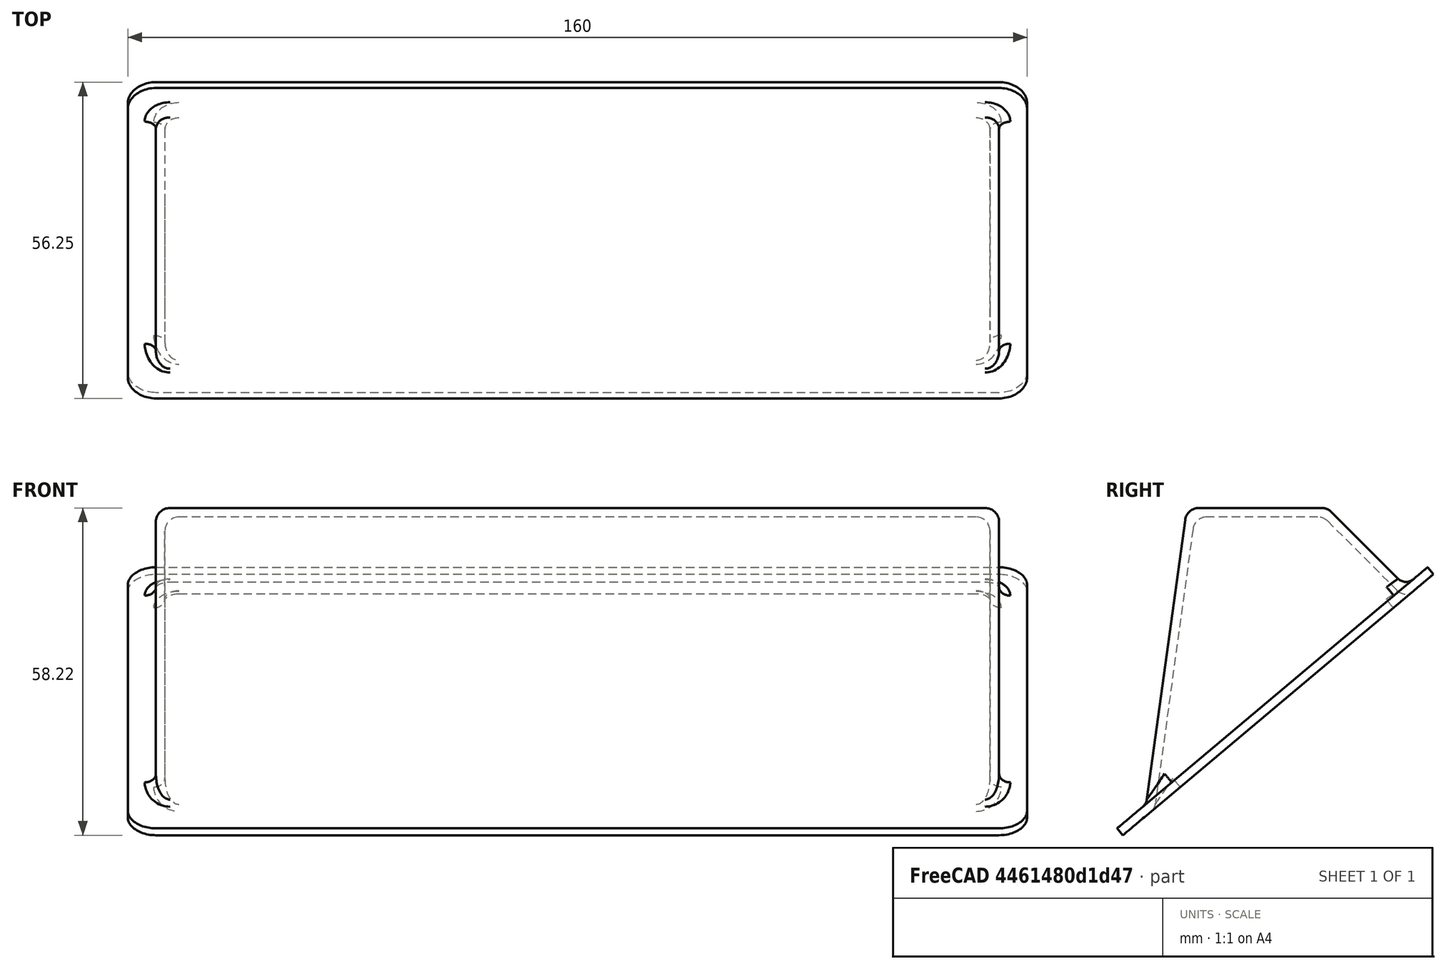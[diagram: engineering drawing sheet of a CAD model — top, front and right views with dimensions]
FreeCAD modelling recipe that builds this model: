
FCSTD DOCUMENT  (FreeCAD 0.22R36807 (Git))
Label: pottle2
License: All rights reserved
LicenseURL: http://en.wikipedia.org/wiki/All_rights_reserved
objects: TechDraw::DrawViewDimension×9, TechDraw::DrawViewBalloon×4, Sketcher::SketchObject×3, PartDesign::FeatureSubtractivePython×3, PartDesign::Pad×2, PartDesign::Fillet×2, Part::FeaturePython×2, App::LinkElement×2, Part::Part2DObjectPython×1, PartDesign::SubShapeBinder×1, PartDesign::Thickness×1, PartDesign::FeaturePython×1, PartDesign::Body×1, TechDraw::DrawSVGTemplate×1, App::DocumentObjectGroup×1, TechDraw::DrawViewPart×1, TechDraw::DrawViewSection×1, TechDraw::DrawPage×1
note: 42 computed .brp shape members not serialized (recipe doc carries the construction recipe); baked Part::Feature solids carry a one-line shape summary decoded from their .brp

FEATURE [Sketcher::SketchObject] Sketch
  FullyConstrained = true
  Placement = pos=(0,0,0) rot=(0.57735,0.57735,0.57735;2.0944rad)
  sketch-geometry (9):
    g0: LineSegment StartX=-31.3593 StartY=11.7819 StartZ=0 EndX=-27.5326 EndY=15 EndZ=0
    g1: LineSegment StartX=-27.5326 StartY=15 StartZ=0 EndX=-12.5 EndY=0 EndZ=0
    g2: LineSegment StartX=-12.5 StartY=0 StartZ=0 EndX=12.5 EndY=0 EndZ=0
    g3: LineSegment StartX=12.5 StartY=0 StartZ=0 EndX=20.0326 EndY=55 EndZ=0
    g4: LineSegment StartX=20.0326 StartY=55 StartZ=0 EndX=23.8593 EndY=58.2181 EndZ=0
    g5: LineSegment StartX=-27.5326 StartY=15 StartZ=0 EndX=20.0326 EndY=55 EndZ=0
    g6: LineSegment StartX=-27.5326 StartY=15 StartZ=0 EndX=-20 EndY=70 EndZ=0
    g7: LineSegment StartX=-20 StartY=70 StartZ=0 EndX=5 EndY=70 EndZ=0
    g8: LineSegment StartX=5 StartY=70 StartZ=0 EndX=20.0326 EndY=55 EndZ=0
  constraints (28):
    c: Coincident(g0,g1)
    c: PointOnObject(g1,g-1)
    c: Coincident(g1,g2)
    c: Coincident(g2,g3)
    c: Coincident(g3,g4)
    c: Equal(g4,g0)
    c: Angle(g0,g1) = 1.65806
    c: Distance(g0,g0) = 5
    c: DistanceX(g2,g2) = 25
    c: Coincident(g5,g0)
    c: Coincident(g5,g3)
    c: Parallel(g0,g5)
    c: Parallel(g5,g4)
    c: DistanceY(g0) = 15
    c: Angle(g2,g1) = 2.35728
    c: Angle(g3,g2) = 1.70691
    c: Distance(g0,g4) = 72.1486
    c: Symmetric(g1,g2,g-2)
    c: Coincident(g0,g6)
    c: Coincident(g6,g7)
    c: Horizontal(g7)
    c: Coincident(g7,g8)
    c: Coincident(g8,g3)
    c: Equal(g8,g1)
    c: Equal(g7,g2)
    c: Equal(g6,g3)
    c: DistanceY(g6) = 70
    c: DistanceX(g7) = 5
FEATURE [Part::Part2DObjectPython] Clone2D  label="Sketch (2D)"  # Draft 2D object (typed FeaturePython)
  Fuse = false
  Objects = -> [Sketch]
  Placement = pos=(7e-15,70.8395,36.5891) rot=(0.57735,0.57735,0.57735;2.0944rad)
  Scale = (1,1,1)
FEATURE [PartDesign::SubShapeBinder] Binder
  BindCopyOnChange = 0
  BindMode = 0
  ClaimChildren = true
  Context = -> Body [Binder.]
  Fuse = false
  MakeFace = true
  OffsetFill = false
  OffsetIntersection = false
  OffsetJoinType = 0
  OffsetOpenResult = false
  PartialLoad = false
  Relative = true
  Support = -> [Sketch]
  _Version = 2
FEATURE [Sketcher::SketchObject] Sketch001
  AttachmentSupport = -> [YZ_Plane]
  ExternalGeometry = -> [Binder]
  FullyConstrained = true
  MapMode = 5
  Placement = pos=(0,0,0) rot=(0.57735,0.57735,0.57735;2.0944rad)
  sketch-geometry (4):
    g0: LineSegment StartX=-12.5 StartY=-1.8e-15 StartZ=0 EndX=12.5 EndY=0 EndZ=0
    g1: LineSegment StartX=12.5 StartY=0 StartZ=0 EndX=20.0326 EndY=55 EndZ=0
    g2: LineSegment StartX=20.0326 StartY=55 StartZ=0 EndX=-27.5326 EndY=15 EndZ=0
    g3: LineSegment StartX=-27.5326 StartY=15 StartZ=0 EndX=-12.5 EndY=-1.8e-15 EndZ=0
  constraints (8):
    c: Coincident(g-3,g0)
    c: Coincident(g0,g-4)
    c: Coincident(g0,g1)
    c: Coincident(g1,g-4)
    c: Coincident(g1,g2)
    c: Coincident(g2,g-3)
    c: Coincident(g2,g3)
    c: Coincident(g3,g0)
FEATURE [PartDesign::Pad] Pad
  Direction = (1,0,0)
  Length = 150
  Length2 = 10
  Midplane = true
  Placement = pos=(0,0,0) rot=(0.57735,0.57735,0.57735;2.0944rad)
  Profile = -> Sketch001
  ReferenceAxis = -> Sketch001 [N_Axis]
  Suppressed = false
  Type = 0
FEATURE [Sketcher::SketchObject] Sketch002
  AttachmentOffset = pos=(0,0,0) rot=(-1,0,0;1.5708rad)
  AttachmentSupport = -> [Binder]
  ExternalGeometry = -> [Binder]
  FullyConstrained = true
  MapMode = 7
  Placement = pos=(0,-27.5326,15) rot=(1,0,0;0.699217rad)
  sketch-geometry (13):
    g0: LineSegment StartX=-75 StartY=-5 StartZ=0 EndX=75 EndY=-5 EndZ=0
    g1: LineSegment StartX=80 StartY=-4e-16 StartZ=0 EndX=80 EndY=62.1486 EndZ=0
    g2: LineSegment StartX=75 StartY=67.1486 StartZ=0 EndX=-75 EndY=67.1486 EndZ=0
    g3: LineSegment StartX=-80 StartY=62.1486 StartZ=0 EndX=-80 EndY=0 EndZ=0
    g4: ArcOfCircle CenterX=-75 CenterY=-5e-16 CenterZ=0 NormalX=0 NormalY=0 NormalZ=1 AngleXU=0 Radius=5 StartAngle=3.14159 EndAngle=4.71239
    g5: ArcOfCircle CenterX=75 CenterY=-3e-16 CenterZ=0 NormalX=0 NormalY=0 NormalZ=1 AngleXU=0 Radius=5 StartAngle=4.71239 EndAngle=6.28319
    g6: ArcOfCircle CenterX=75 CenterY=62.1486 CenterZ=0 NormalX=0 NormalY=0 NormalZ=1 AngleXU=0 Radius=5 StartAngle=-9e-16 EndAngle=1.5708
    g7: ArcOfCircle CenterX=-75 CenterY=62.1486 CenterZ=0 NormalX=0 NormalY=0 NormalZ=1 AngleXU=0 Radius=5 StartAngle=1.5708 EndAngle=3.14159
    g8: GeomPoint X=-80 Y=-5 Z=0
    g9: GeomPoint X=80 Y=67.1486 Z=0
    g10: LineSegment StartX=0 StartY=62.1486 StartZ=0 EndX=0 EndY=67.1486 EndZ=0
    g11: LineSegment StartX=0 StartY=0 StartZ=0 EndX=0 EndY=-5 EndZ=0
    g12: GeomPoint X=0 Y=31.0743 Z=0
  constraints (31):
    c: Tangent(g0,g4) = -1.5708
    c: Tangent(g0,g5) = -1.5708
    c: Tangent(g1,g5) = -1.5708
    c: Tangent(g1,g6) = -1.5708
    c: Tangent(g2,g6) = -1.5708
    c: Tangent(g2,g7) = -1.5708
    c: Tangent(g3,g7) = -1.5708
    c: Tangent(g3,g4) = -1.5708
    c: Horizontal(g0)
    c: Horizontal(g2)
    c: Vertical(g1)
    c: Vertical(g3)
    c: Equal(g4,g5)
    c: Equal(g5,g6)
    c: Equal(g6,g7)
    c: PointOnObject(g8,g0)
    c: PointOnObject(g8,g3)
    c: PointOnObject(g9,g1)
    c: PointOnObject(g9,g2)
    c: Radius(g5) = 5
    c: Coincident(g10,g-3)
    c: PointOnObject(g10,g2)
    c: Coincident(g11,g-1)
    c: PointOnObject(g11,g0)
    c: Vertical(g11)
    c: Equal(g11,g10)
    c: PointOnObject(g12,g-2)
    c: Symmetric(g8,g9,g12)
    c: DistanceX(g8,g9) = 160
    c: DistanceY(g11,g11) = 5
    c: Vertical(g10)
FEATURE [PartDesign::Thickness] Thickness
  Base = -> Pad [Face3]
  BaseFeature = -> Pad
  Intersection = false
  Join = 0
  Mode = 0
  Reversed = true
  SupportTransform = false
  Suppressed = false
  Value = 1.6
FEATURE [PartDesign::FeatureSubtractivePython] PDW_Sub  # link proxy (typed FeaturePython)
  BaseFeature = -> Thickness
  Body = Body
  ClaimChildren = false
  EditPlacementAdjustments = false
  Enabled = 1
  LinkedObject = -> Thickness
  MeshTolerance = 0.1
  PatternBase = -> Pad
  PatternBaseOffset = 0
  PatternBaseScale = 1
  PatternBaseScaleXYZ = (1,1,1)
  PatternOffsetCut = false
  PatternOffsetIntersection = false
  PatternOffsetJoin = 0
  PatternOffsetMode = 0
  PatternOffsetSelfIntersection = false
  PatternOperation = 0
  PatternOperationDefault = None
  PatternScaleCut = false
  PatternShapeOffset = 0
  PatternShapeScale = 1
  PatternShapeScaleXYZ = (1,1,1)
  PatternTool = -> Thickness
  PatternToolOffset = 0
  PatternToolScale = 1
  PatternToolScaleXYZ = (1,1,1)
  RefineMesh = true
  ShapeManagement = 1
  ShowMeshProps = false
  ShowOffsetProps = false
  ShowScaleProps = false
  ShowWarnings = true
  Suppressed = false
  TipBase = -> Pad
  TipBaseOffset = 0
  TipBaseScale = 1
  TipBaseScaleXYZ = (1,1,1)
  TipOffsetCut = false
  TipOffsetIntersection = false
  TipOffsetJoin = 0
  TipOffsetMode = 0
  TipOffsetSelfIntersection = false
  TipOperation = 1
  TipOperationDefault = Cut
  TipScaleCut = false
  TipShapeOffset = 0
  TipShapeScale = 1
  TipShapeScaleXYZ = (1,1,1)
  TipTool = -> Thickness
  TipToolOffset = 0
  TipToolScale = 1
  TipToolScaleXYZ = (1,1,1)
  Type = Subtractive
  UsePatternBaseAddSubShape = false
  UsePatternToolAddSubShape = true
  UseTipBaseAddSubShape = false
  UseTipToolAddSubShape = false
  Version = 0.2023.08.13
FEATURE [PartDesign::FeatureSubtractivePython] PDW_Sub001  # link proxy (typed FeaturePython)
  BaseFeature = -> PDW_Sub
  Body = Body
  ClaimChildren = false
  EditPlacementAdjustments = false
  Enabled = 1
  LinkedObject = -> PDW_Sub
  MeshTolerance = 0.1
  PatternBase = -> Thickness
  PatternBaseOffset = 0
  PatternBaseScale = 1
  PatternBaseScaleXYZ = (1,1,1)
  PatternOffsetCut = false
  PatternOffsetIntersection = false
  PatternOffsetJoin = 0
  PatternOffsetMode = 0
  PatternOffsetSelfIntersection = false
  PatternOperation = 0
  PatternOperationDefault = None
  PatternScaleCut = false
  PatternShapeOffset = 0
  PatternShapeScale = 1
  PatternShapeScaleXYZ = (1,1,1)
  PatternTool = -> PDW_Sub
  PatternToolOffset = 0
  PatternToolScale = 1
  PatternToolScaleXYZ = (1,1,1)
  RefineMesh = true
  ShapeManagement = 0
  ShowMeshProps = false
  ShowOffsetProps = false
  ShowScaleProps = false
  ShowWarnings = true
  Suppressed = false
  TipBase = -> Thickness
  TipBaseOffset = 0
  TipBaseScale = 1
  TipBaseScaleXYZ = (1,1,1)
  TipOffsetCut = false
  TipOffsetIntersection = false
  TipOffsetJoin = 0
  TipOffsetMode = 0
  TipOffsetSelfIntersection = false
  TipOperation = 1
  TipOperationDefault = Cut
  TipScaleCut = false
  TipShapeOffset = 0
  TipShapeScale = 1
  TipShapeScaleXYZ = (1,1,1)
  TipTool = -> PDW_Sub
  TipToolOffset = 0
  TipToolScale = 1
  TipToolScaleXYZ = (1,1,1)
  Type = Subtractive
  UsePatternBaseAddSubShape = false
  UsePatternToolAddSubShape = true
  UseTipBaseAddSubShape = false
  UseTipToolAddSubShape = true
  Version = 0.2023.08.13
FEATURE [PartDesign::Pad] Pad001
  BaseFeature = -> PDW_Sub001
  Direction = (0,-0.643619,0.765346)
  Length = 1.6
  Length2 = 10
  Profile = -> Sketch002
  ReferenceAxis = -> Sketch002 [N_Axis]
  Refine = true
  Reversed = true
  Suppressed = false
  Type = 0
  expr: Length = <<Thickness>>.Value
FEATURE [PartDesign::FeatureSubtractivePython] PDW_Sub002  # link proxy (typed FeaturePython)
  BaseFeature = -> Pad001
  Body = Body
  ClaimChildren = false
  EditPlacementAdjustments = false
  Enabled = 1
  LinkedObject = -> PDW_Sub
  MeshTolerance = 0.1
  PatternBase = -> Pad001
  PatternBaseOffset = 0
  PatternBaseScale = 1
  PatternBaseScaleXYZ = (1,1,1)
  PatternOffsetCut = false
  PatternOffsetIntersection = false
  PatternOffsetJoin = 0
  PatternOffsetMode = 0
  PatternOffsetSelfIntersection = false
  PatternOperation = 0
  PatternOperationDefault = None
  PatternScaleCut = false
  PatternShapeOffset = 0
  PatternShapeScale = 1
  PatternShapeScaleXYZ = (1,1,1)
  PatternTool = -> PDW_Sub
  PatternToolOffset = 0
  PatternToolScale = 1
  PatternToolScaleXYZ = (1,1,1)
  RefineMesh = false
  ShapeManagement = 1
  ShowMeshProps = false
  ShowOffsetProps = false
  ShowScaleProps = false
  ShowWarnings = true
  Suppressed = false
  TipBase = -> Pad001
  TipBaseOffset = 0
  TipBaseScale = 1
  TipBaseScaleXYZ = (1,1,1)
  TipOffsetCut = false
  TipOffsetIntersection = false
  TipOffsetJoin = 0
  TipOffsetMode = 0
  TipOffsetSelfIntersection = false
  TipOperation = 1
  TipOperationDefault = Cut
  TipScaleCut = false
  TipShapeOffset = 0
  TipShapeScale = 1
  TipShapeScaleXYZ = (1,1,1)
  TipTool = -> PDW_Sub
  TipToolOffset = 0
  TipToolScale = 1
  TipToolScaleXYZ = (1,1,1)
  Type = Subtractive
  UsePatternBaseAddSubShape = false
  UsePatternToolAddSubShape = true
  UseTipBaseAddSubShape = false
  UseTipToolAddSubShape = false
  Version = 0.2023.08.13
FEATURE [PartDesign::FeaturePython] Extend  # WARN: FeaturePython — macro-defined, semantics opaque (R4)
  BaseFeature = -> PDW_Sub002
  Offset = 0.02
  Refine = true
  Suppressed = false
  UseSubtraction = false
  baseObject = -> PDW_Sub002 [Face1]
  gap1 = 0
  gap2 = 0
  length = 0
FEATURE [PartDesign::Fillet] Fillet
  Base = -> Extend [Edge46,Edge43,Edge42,Edge45,Edge48,Edge47,Edge44,Edge41,Edge6,Edge4,Edge10,Edge2,Edge8,Edge3,Edge1,Edge5]
  BaseFeature = -> Extend
  Radius = 2.5
  SupportTransform = false
  Suppressed = false
  UseAllEdges = false
FEATURE [PartDesign::Fillet] Fillet001
  Base = -> Fillet [Edge69,Edge26]
  BaseFeature = -> Fillet
  Radius = 2
  SupportTransform = false
  Suppressed = false
  UseAllEdges = false
FEATURE [PartDesign::Body] Body
  Group = -> [Sketch001,Binder,Pad,Sketch002,Thickness,PDW_Sub,PDW_Sub001,Pad001,PDW_Sub002,Extend,Fillet,Fillet001]
  Origin = -> Origin
  Tip = -> Fillet001
FEATURE [Part::FeaturePython] Clone  label="Body001"  # Draft clone (typed FeaturePython)
  AttacherType = Attacher::AttachEngine3D
  Fuse = false
  Objects = -> [Body]
  Placement = pos=(0,-7.3235,70) rot=(1,0,0;3.14159rad)
  Scale = (1,1,1)
FEATURE [TechDraw::DrawSVGTemplate] Template
  Height = 210
  Orientation = 1
  Template = <path>
  Width = 297
FEATURE [App::DocumentObjectGroup] Group
FEATURE [App::LinkElement] Array_i0
  LinkedObject = -> Body
  _LinkOwner = 2197
FEATURE [App::LinkElement] Array_i1
  LinkPlacement = pos=(0,55.2187,46.4362) rot=(0,0,1;0rad)
  LinkedObject = -> Body
  Placement = pos=(0,55.2187,46.4362) rot=(0,0,1;0rad)
  _LinkOwner = 2197
FEATURE [Part::FeaturePython] Array  # Draft array (typed FeaturePython)
  AlwaysSyncPlacement = false
  Angle = 360
  ArrayType = 0
  Axis = (0,0,1)
  Base = -> Body
  Center = (0,0,0)
  Count = 2
  ElementList = -> [Array_i0,Array_i1]
  ExpandArray = true
  Fuse = false
  IntervalAxis = (0,0,0)
  IntervalX = (100,0,0)
  IntervalY = (0,55.2187,46.4362)
  IntervalZ = (0,0,100)
  NumberCircles = 3
  NumberPolar = 5
  NumberX = 1
  NumberY = 2
  NumberZ = 1
  RadialDistance = 50
  Symmetry = 1
  TangentialDistance = 25
FEATURE [TechDraw::DrawViewPart] View
  CoarseView = false
  Direction = (0,-0.643619,0.765346)
  Focus = 100
  HardHidden = false
  IsoCount = 0
  IsoHidden = false
  IsoVisible = false
  LockPosition = false
  Perspective = false
  Rotation = 90
  ScaleType = 0
  ScrubCount = 0
  SeamHidden = false
  SeamVisible = true
  SmoothHidden = false
  SmoothVisible = true
  Source = -> [Array]
  X = 199.811
  XDirection = (1,0,0)
  Y = 104.476
FEATURE [TechDraw::DrawViewSection] SectionView  label="Section  - "
  BaseView = -> View
  CoarseView = false
  CutSurfaceDisplay = 2
  Direction = (-1,-1e-16,-1e-16)
  FileGeomPattern = <path>
  FileHatchPattern = <path>
  Focus = 100
  FuseBeforeCut = false
  HardHidden = false
  HatchOffset = (0,0,0)
  HatchRotation = 0
  HatchScale = 1
  IsoCount = 0
  IsoHidden = false
  IsoVisible = false
  LockPosition = false
  NameGeomPattern = Diamond
  Perspective = false
  Rotation = -90
  ScaleType = 0
  ScrubCount = 0
  SeamHidden = false
  SeamVisible = true
  SectionDirection = 4
  SectionLineStretch = 1
  SectionNormal = (-1,-1e-16,-1e-16)
  SectionOrigin = (0,57.973,21.06)
  SmoothHidden = false
  SmoothVisible = true
  Source = -> [Array]
  TrimAfterCut = false
  UsePreviousCut = false
  X = 48.5
  XDirection = (1e-16,-0.765346,-0.643619)
  Y = 105
FEATURE [TechDraw::DrawViewDimension] Dimension001
  AngleOverride = false
  Arbitrary = false
  ArbitraryTolerances = false
  BoxCorners = (2) [(-18.2145,-72.1486,-1e-07),(18.2145,72.1486,1e-07)]
  EqualTolerance = true
  ExtensionAngle = 0
  FormatSpec = %.2w
  FormatSpecOverTolerance = %+.2w
  FormatSpecUnderTolerance = %+.2w
  Inverted = false
  LineAngle = 0
  LockPosition = false
  MeasureType = 1
  OverTolerance = 0
  References2D = -> [SectionView]
  Rotation = 0
  ScaleType = 0
  TheoreticalExact = false
  Type = 0
  UnderTolerance = 0
  X = 5.9692
  Y = -68.9548
FEATURE [TechDraw::DrawViewDimension] Dimension002
  AngleOverride = false
  Arbitrary = false
  ArbitraryTolerances = false
  BoxCorners = (2) [(-18.2145,-72.1486,-1e-07),(18.2145,72.1486,1e-07)]
  EqualTolerance = true
  ExtensionAngle = 0
  FormatSpec = %.2w
  FormatSpecOverTolerance = %+.2w
  FormatSpecUnderTolerance = %+.2w
  Inverted = false
  LineAngle = 0
  LockPosition = false
  MeasureType = 1
  OverTolerance = 0
  References2D = -> [SectionView]
  Rotation = 0
  ScaleType = 0
  TheoreticalExact = false
  Type = 0
  UnderTolerance = 0
  X = -16.8596
  Y = -56.3773
FEATURE [TechDraw::DrawViewDimension] Dimension003
  AngleOverride = false
  Arbitrary = false
  ArbitraryTolerances = false
  BoxCorners = (2) [(-18.2145,-72.1486,-1e-07),(18.2145,72.1486,1e-07)]
  EqualTolerance = true
  ExtensionAngle = 0
  FormatSpec = %.2w
  FormatSpecOverTolerance = %+.2w
  FormatSpecUnderTolerance = %+.2w
  Inverted = false
  LineAngle = 0
  LockPosition = false
  MeasureType = 1
  OverTolerance = 0
  References2D = -> [SectionView]
  Rotation = 0
  ScaleType = 0
  TheoreticalExact = false
  Type = 0
  UnderTolerance = 0
  X = -9.73978
  Y = -20.5311
FEATURE [TechDraw::DrawViewDimension] Dimension005
  AngleOverride = false
  Arbitrary = false
  ArbitraryTolerances = false
  BoxCorners = (2) [(-18.2145,-72.1486,-1e-07),(18.2145,72.1486,1e-07)]
  EqualTolerance = true
  ExtensionAngle = 0
  FormatSpec = %.2w
  FormatSpecOverTolerance = %+.2w
  FormatSpecUnderTolerance = %+.2w
  Inverted = false
  LineAngle = 0
  LockPosition = false
  MeasureType = 1
  OverTolerance = 0
  References2D = -> [SectionView]
  Rotation = 0
  ScaleType = 0
  TheoreticalExact = false
  Type = 6
  UnderTolerance = 0
  X = 11.5996
  Y = 3.17897
FEATURE [TechDraw::DrawViewDimension] Dimension006
  AngleOverride = false
  Arbitrary = false
  ArbitraryTolerances = false
  BoxCorners = (2) [(-18.2145,-72.1486,-1e-07),(18.2145,72.1486,1e-07)]
  EqualTolerance = true
  ExtensionAngle = 0
  FormatSpec = %.2w
  FormatSpecOverTolerance = %+.2w
  FormatSpecUnderTolerance = %+.2w
  Inverted = false
  LineAngle = 0
  LockPosition = false
  MeasureType = 1
  OverTolerance = 0
  References2D = -> [SectionView]
  Rotation = 0
  ScaleType = 0
  TheoreticalExact = false
  Type = 6
  UnderTolerance = 0
  X = 1.03381
  Y = 22.7332
FEATURE [TechDraw::DrawViewDimension] Dimension007
  AngleOverride = false
  Arbitrary = false
  ArbitraryTolerances = false
  BoxCorners = (2) [(-18.2145,-72.1486,-1e-07),(18.2145,72.1486,1e-07)]
  EqualTolerance = true
  ExtensionAngle = 0
  FormatSpec = %.2w
  FormatSpecOverTolerance = %+.2w
  FormatSpecUnderTolerance = %+.2w
  Inverted = false
  LineAngle = 0
  LockPosition = false
  MeasureType = 1
  OverTolerance = 0
  References2D = -> [SectionView]
  Rotation = 0
  ScaleType = 0
  TheoreticalExact = false
  Type = 6
  UnderTolerance = 0
  X = -1.27528
  Y = -40.6079
FEATURE [TechDraw::DrawViewDimension] Dimension008
  AngleOverride = false
  Arbitrary = false
  ArbitraryTolerances = false
  BoxCorners = (2) [(-18.2145,-72.1486,-1e-07),(18.2145,72.1486,1e-07)]
  EqualTolerance = true
  ExtensionAngle = 0
  FormatSpec = %.2w
  FormatSpecOverTolerance = %+.2w
  FormatSpecUnderTolerance = %+.2w
  Inverted = false
  LineAngle = 0
  LockPosition = false
  MeasureType = 1
  OverTolerance = 0
  References2D = -> [SectionView]
  Rotation = 0
  ScaleType = 0
  TheoreticalExact = false
  Type = 6
  UnderTolerance = 0
  X = 13.2309
  Y = 84.7426
FEATURE [TechDraw::DrawViewBalloon] Balloon
  BubbleShape = 3
  EndType = 0
  EndTypeScale = 1
  KinkLength = 5
  LockPosition = false
  OriginX = -67.4739
  OriginY = 76.2607
  Rotation = 0
  ScaleType = 0
  ShapeScale = 1
  SourceView = -> View
  Text = Кнопка
  TextWrapLen = -1
  X = -91.1181
  Y = 96.5969
FEATURE [TechDraw::DrawViewBalloon] Balloon001
  BubbleShape = 3
  EndType = 0
  EndTypeScale = 1
  KinkLength = 5
  LockPosition = false
  OriginX = -66.8363
  OriginY = -75.0507
  Rotation = 0
  ScaleType = 0
  ShapeScale = 1
  SourceView = -> View
  Text = Кнопка
  TextWrapLen = -1
  X = -43.8479
  Y = -87.7825
FEATURE [TechDraw::DrawViewBalloon] Balloon002
  BubbleShape = 0
  EndType = 0
  EndTypeScale = 1
  KinkLength = 5
  LockPosition = false
  OriginX = -17.6808
  OriginY = 10.3544
  Rotation = 0
  ScaleType = 0
  ShapeScale = 0.1
  SourceView = -> View
  TextWrapLen = -1
  X = -17.1256
  Y = 82.39
FEATURE [TechDraw::DrawViewBalloon] Balloon003
  BubbleShape = 3
  EndType = 0
  EndTypeScale = 1
  KinkLength = 5
  LockPosition = false
  OriginX = 56.7885
  OriginY = 47.8324
  Rotation = 0
  ScaleType = 0
  ShapeScale = 1
  SourceView = -> View
  Text = Вставить текст "Моя Микрозелень"
  TextWrapLen = -1
  X = 3.29934
  Y = 88.8808
FEATURE [TechDraw::DrawViewDimension] Dimension
  AngleOverride = false
  Arbitrary = false
  ArbitraryTolerances = false
  BoxCorners = (2) [(-72.1486,-80,-1e-07),(72.1486,80,1e-07)]
  EqualTolerance = true
  ExtensionAngle = 0
  FormatSpec = %.2w
  FormatSpecOverTolerance = %+.2w
  FormatSpecUnderTolerance = %+.2w
  Inverted = false
  LineAngle = 0
  LockPosition = false
  MeasureType = 1
  OverTolerance = 0
  References2D = -> [View]
  Rotation = 0
  ScaleType = 0
  TheoreticalExact = false
  Type = 0
  UnderTolerance = 0
  X = 80.0111
  Y = 12.0295
FEATURE [TechDraw::DrawViewDimension] Dimension009
  AngleOverride = false
  Arbitrary = false
  ArbitraryTolerances = false
  BoxCorners = (2) [(-18.2145,-72.1486,-1e-07),(18.2145,72.1486,1e-07)]
  EqualTolerance = true
  ExtensionAngle = 0
  FormatSpec = %.2w
  FormatSpecOverTolerance = %+.2w
  FormatSpecUnderTolerance = %+.2w
  Inverted = false
  LineAngle = 0
  LockPosition = false
  MeasureType = 1
  OverTolerance = 0
  References2D = -> [SectionView]
  Rotation = 0
  ScaleType = 0
  TheoreticalExact = false
  Type = 2
  UnderTolerance = 0
  X = 28.3158
  Y = -31.2857
FEATURE [TechDraw::DrawPage] Page
  KeepUpdated = true
  NextBalloonIndex = 5
  ProjectionType = 0
  Template = -> Template
  Views = -> [View,SectionView,Dimension001,Dimension002,Dimension003,Dimension005,Dimension006,Dimension007,Dimension008,Balloon,Balloon001,Balloon002,Balloon003,Dimension,Dimension009]
note: 3 file-system paths scrubbed to <path> (originals preserved in the JSON sidecar)
